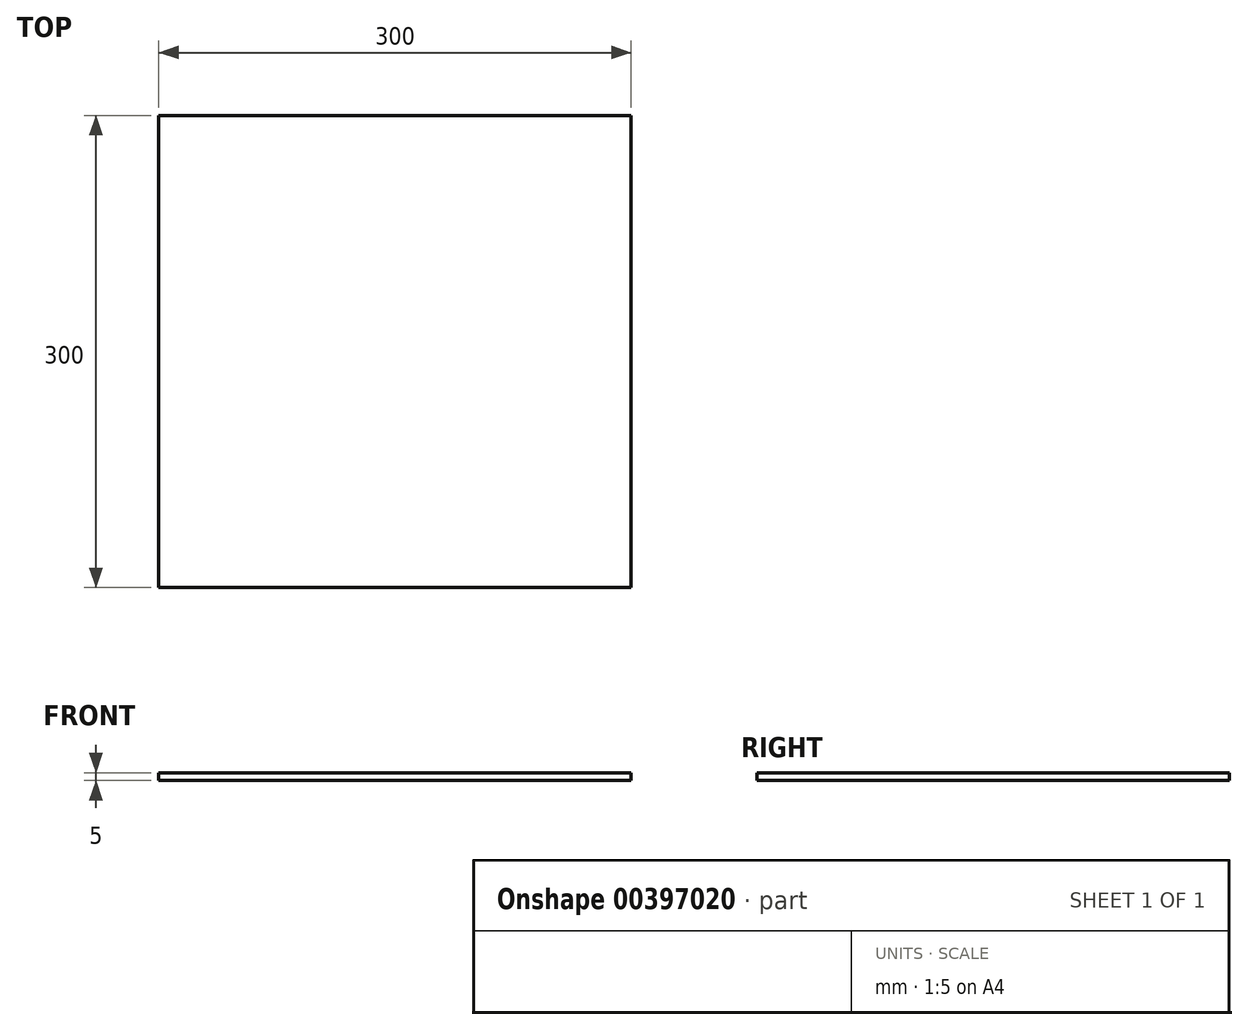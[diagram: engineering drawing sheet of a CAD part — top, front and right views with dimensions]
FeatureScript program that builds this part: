
annotation { "Feature Type Name" : "Feature", "Feature Type Description" : "" }
export const myFeature = defineFeature(function(context is Context, id is Id, definition is map)
    precondition{}
    {
        {
            var Q0;
            Q0=qCreatedBy(makeId("Top.planeOp"),FACE);
            var sketch = newSketch(context, id + "F0", { "sketchPlane" : qUnion([Q0])});
            skLineSegment(sketch, "E0.bottom", {"start": v(0, 0) * mm, "end": v(300, 0) * mm});
            skLineSegment(sketch, "E0.top", {"start": v(0, 300) * mm, "end": v(300, 300) * mm});
            skLineSegment(sketch, "E0.left", {"start": v(0, 0) * mm, "end": v(0, 300) * mm});
            skLineSegment(sketch, "E0.right", {"start": v(300, 0) * mm, "end": v(300, 300) * mm});
            skSolve(sketch);
        }
        {
            var Q0;
            Q0 = qSketchRegion(id + "F0", true);
            extrude(context, id + "F1", {"entities" : qUnion([Q0]), "depth" : 5 * mm});
        }
    });
